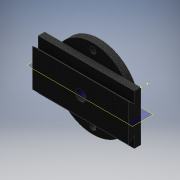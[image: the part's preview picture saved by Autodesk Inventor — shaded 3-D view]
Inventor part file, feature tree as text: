
AUTODESK INVENTOR PART (.ipt)
format: ipt  version: 2016 (Build 200138000, 138)  size: 177,152 bytes
history: native  units: mm
features: sketch x8, extrude x6, plane x1
ambient origin geometry x8: Origin, YZ Plane, XZ Plane, XY Plane, X Axis, Y Axis, Z Axis, Center Point
bodies: Solid1 (feature_tree)
feature tree (15):
  extrude  "Extrusion1"  Depth=19.0mm
  sketch  "Sketch2"  dims[d8=165.2mm d9=0.0mm d10=14.0mm]
  extrude  "Extrusion2"  Depth=165.2mm
  extrude  "Extrusion3"  Depth=11.5mm TaperAngle=0.0deg
  extrude  "Extrusion4"  Depth=73.75mm TaperAngle=0.0deg
  sketch  "Sketch6"  dims[d19=5.4mm d20=5.4mm]
  extrude  "Extrusion5"  Depth=6.0mm
  extrude  "Extrusion6"  Depth=5.4mm
  plane  "Work Plane1"
  sketch  "Sketch1"  dims[d1=85.6mm d7=19.0mm]
  sketch  "Sketch3"  dims[d11=68.3mm d12=11.5mm d13=0.0mm]
  sketch  "Sketch4"  dims[d14=18.3mm d15=73.75mm d16=0.0mm]
  sketch  "Sketch5"  dims[d17=6.0mm d18=6.0mm]
  sketch  "Sketch7"  dims[d21=73.75mm d22=0.0mm]
  sketch  "Sketch8"  dims[d23=6.9mm d24=10.8mm d25=6.0mm d26=0.0mm d27=6.2mm d28=22.8mm d29=0.0mm d30=8.726646mm d31=19.0mm d32=8.726646mm d33=10.0mm]
